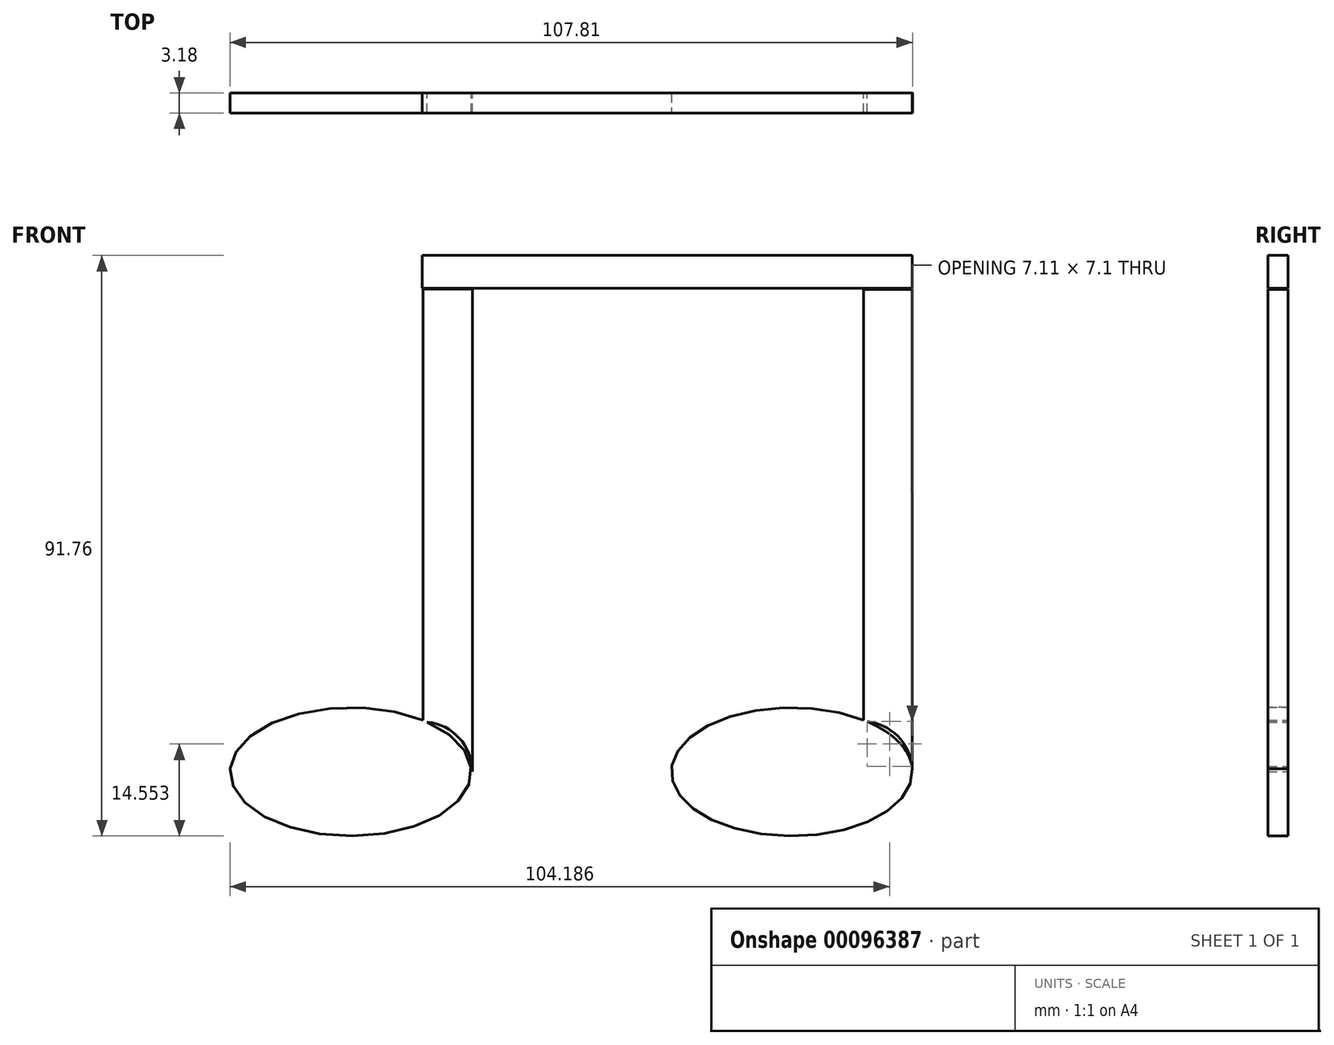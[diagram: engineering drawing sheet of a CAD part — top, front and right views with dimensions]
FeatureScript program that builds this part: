
annotation { "Feature Type Name" : "Feature", "Feature Type Description" : "" }
export const myFeature = defineFeature(function(context is Context, id is Id, definition is map)
    precondition{}
    {
        {
            var Q0;
            Q0=qCreatedBy(makeId("Front.planeOp"),FACE);
            var sketch = newSketch(context, id + "F0", { "sketchPlane" : qUnion([Q0])});
            skEllipse(sketch, "E0", {"center": v(-31.75, 0) * mm, "majorRadius": 19.05 * mm, "minorRadius": 10.16 * mm, "majorAxis": v(1, 0)});
            skSolve(sketch);
        }
        {
            var Q0;
            Q0=qCreatedBy(makeId("Front.planeOp"),FACE);
            var sketch = newSketch(context, id + "F1", { "sketchPlane" : qUnion([Q0])});
            skEllipse(sketch, "E1", {"center": v(37.96, 0) * mm, "majorRadius": 19.05 * mm, "minorRadius": 10.16 * mm, "majorAxis": v(-1, 0)});
            skSolve(sketch);
        }
        {
            var Q0;
            Q0=qCreatedBy(makeId("Front.planeOp"),FACE);
            var sketch = newSketch(context, id + "F2", { "sketchPlane" : qUnion([Q0])});
            skLineSegment(sketch, "E2", {"start": v(-12.53, 0) * mm, "end": v(-12.53, 76.32) * mm});
            skLineSegment(sketch, "E3", {"start": v(-12.53, 76.32) * mm, "end": v(-20.3, 76.32) * mm});
            skLineSegment(sketch, "E4", {"start": v(-20.3, 76.32) * mm, "end": v(-20.3, 7.9) * mm});
            skArc(sketch, "E5", {"start": v(-12.53, 0) * mm, "mid": v(-14.8, 5.54) * mm, "end": v(-20.3, 7.9) * mm});
            skSolve(sketch);
        }
        {
            var Q0;
            Q0=qCreatedBy(makeId("Front.planeOp"),FACE);
            var sketch = newSketch(context, id + "F3", { "sketchPlane" : qUnion([Q0])});
            skLineSegment(sketch, "E6", {"start": v(56.98, 0) * mm, "end": v(56.98, 76.2) * mm});
            skLineSegment(sketch, "E7", {"start": v(56.98, 76.2) * mm, "end": v(49.25, 76.2) * mm});
            skLineSegment(sketch, "E8", {"start": v(49.25, 76.2) * mm, "end": v(49.25, 7.98) * mm});
            skArc(sketch, "E9", {"start": v(56.98, 0) * mm, "mid": v(54.73, 5.56) * mm, "end": v(49.25, 7.98) * mm});
            skSolve(sketch);
        }
        {
            var Q0;
            Q0=qCreatedBy(makeId("Front.planeOp"),FACE);
            var sketch = newSketch(context, id + "F4", { "sketchPlane" : qUnion([Q0])});
            skLineSegment(sketch, "E10", {"start": v(-20.46, 76.42) * mm, "end": v(56.99, 76.42) * mm});
            skLineSegment(sketch, "E11", {"start": v(56.99, 76.42) * mm, "end": v(56.99, 81.6) * mm});
            skLineSegment(sketch, "E12", {"start": v(56.99, 81.6) * mm, "end": v(-20.46, 81.6) * mm});
            skLineSegment(sketch, "E13", {"start": v(-20.46, 81.6) * mm, "end": v(-20.46, 76.42) * mm});
            skSolve(sketch);
        }
        {
            var Q0;
            Q0 = qSketchRegion(id + "F0", true);
            extrude(context, id + "F5", {"entities" : qUnion([Q0]), "endBound" : BoundingType.SYMMETRIC, "depth" : 3.17 * mm});
        }
        {
            var Q0;
            Q0 = qSketchRegion(id + "F1", true);
            extrude(context, id + "F6", {"entities" : qUnion([Q0]), "endBound" : BoundingType.SYMMETRIC, "depth" : 3.17 * mm});
        }
        {
            var Q0;
            Q0 = qSketchRegion(id + "F2", true);
            extrude(context, id + "F7", {"entities" : qUnion([Q0]), "operationType" : NewBodyOperationType.ADD, "endBound" : BoundingType.SYMMETRIC, "depth" : 3.17 * mm});
        }
        {
            var Q0;
            Q0 = qSketchRegion(id + "F3", true);
            extrude(context, id + "F8", {"entities" : qUnion([Q0]), "operationType" : NewBodyOperationType.ADD, "endBound" : BoundingType.SYMMETRIC, "depth" : 3.17 * mm});
        }
        {
            var Q0;
            Q0 = qSketchRegion(id + "F4", true);
            extrude(context, id + "F9", {"entities" : qUnion([Q0]), "endBound" : BoundingType.SYMMETRIC, "depth" : 3.17 * mm});
        }
    });
